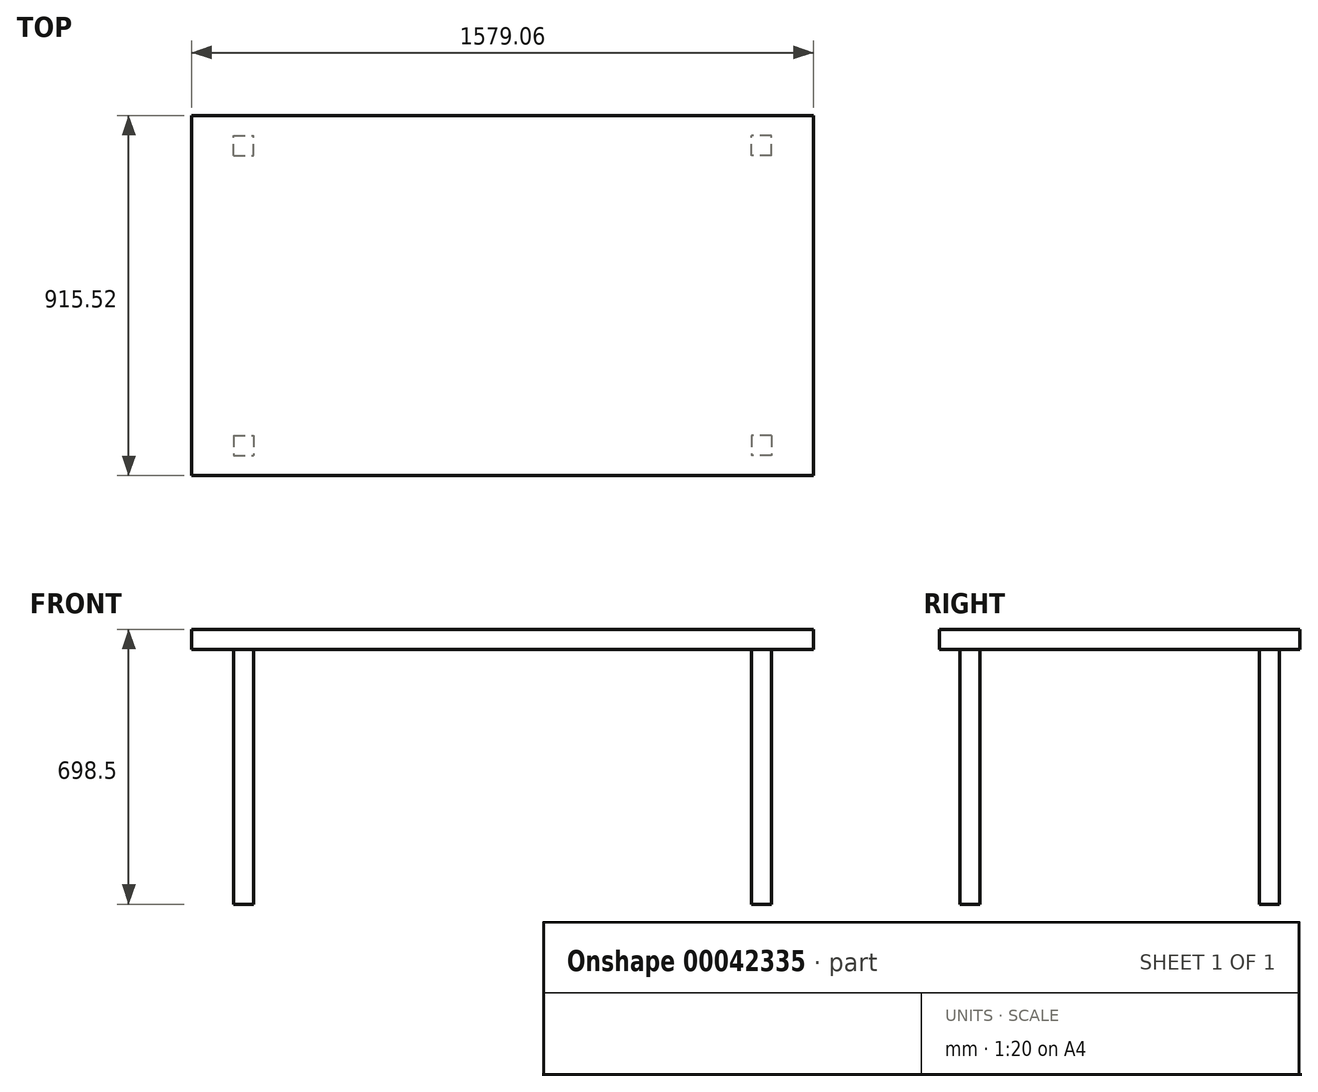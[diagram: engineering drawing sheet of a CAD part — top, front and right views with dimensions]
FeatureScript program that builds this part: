
annotation { "Feature Type Name" : "Feature", "Feature Type Description" : "" }
export const myFeature = defineFeature(function(context is Context, id is Id, definition is map)
    precondition{}
    {
        {
            var Q0;
            Q0=qCreatedBy(makeId("Top.planeOp"),FACE);
            var sketch = newSketch(context, id + "F0", { "sketchPlane" : qUnion([Q0])});
            skLineSegment(sketch, "E0.bottom", {"start": v(-734.47, 457.76) * mm, "end": v(789.53, 457.76) * mm});
            skLineSegment(sketch, "E0.top", {"start": v(-734.47, -456.64) * mm, "end": v(789.53, -456.64) * mm});
            skLineSegment(sketch, "E0.left", {"start": v(-734.47, 457.76) * mm, "end": v(-734.47, -456.64) * mm});
            skLineSegment(sketch, "E0.right", {"start": v(789.53, 457.76) * mm, "end": v(789.53, -456.64) * mm});
            skSolve(sketch);
        }
        {
            var Q0;
            Q0=qSketchRegion(id+"F0",true);
            extrude(context, id + "F1", {"entities" : qUnion([Q0]), "depth" : 50.8 * mm});
        }
        {
            var Q0;
            Q0=makeQuery(id+"F1.opExtrude","CAP_FACE",FACE,{"disambiguationData":[OSD([sQuery(id+"F0.wireOp",EDGE,"E0.bottom"),sQuery(id+"F0.wireOp",EDGE,"E0.top"),sQuery(id+"F0.wireOp",EDGE,"E0.left"),sQuery(id+"F0.wireOp",EDGE,"E0.right")])],"isStart":false});
            var sketch = newSketch(context, id + "F2", { "sketchPlane" : qUnion([Q0])});
            skLineSegment(sketch, "E1.bottom", {"start": v(-683.67, -355.04) * mm, "end": v(-632.87, -355.04) * mm});
            skLineSegment(sketch, "E1.top", {"start": v(-683.67, -405.84) * mm, "end": v(-632.87, -405.84) * mm});
            skLineSegment(sketch, "E1.left", {"start": v(-683.67, -355.04) * mm, "end": v(-683.67, -405.84) * mm});
            skLineSegment(sketch, "E1.right", {"start": v(-632.87, -355.04) * mm, "end": v(-632.87, -405.84) * mm});
            skSolve(sketch);
        }
        {
            var Q0;
            Q0=makeQuery(id+"F2.imprint","IMPRINT",FACE,{"disambiguationData":[TD([[makeQuery(id+"F2.imprint","IMPRINT",EDGE,{"derivedFrom":sQuery(id+"F2.wireOp",EDGE,"E1.bottom")}),-1.0]])]});
            extrude(context, id + "F3", {"entities" : qUnion([Q0]), "operationType" : NewBodyOperationType.ADD, "oppositeDirection" : true, "depth" : 698.5 * mm});
        }
        {
            var Q0;
            Q0=makeQuery(id+"F1.opExtrude","SWEPT_BODY",BODY,{"disambiguationData":[OSD([sQuery(id+"F0.wireOp",EDGE,"E0.bottom"),sQuery(id+"F0.wireOp",EDGE,"E0.top"),sQuery(id+"F0.wireOp",EDGE,"E0.left"),sQuery(id+"F0.wireOp",EDGE,"E0.right")])]});
            var Q1;
            Q1=qCreatedBy(makeId("Front.planeOp"),FACE);
            mirror(context, id + "F4", {"operationType" : NewBodyOperationType.ADD, "entities" : qUnion([Q0]), "mirrorPlane" : qUnion([Q1])});
        }
        {
            var Q0;
            Q0=makeQuery(id+"F1.opExtrude","SWEPT_BODY",BODY,{"disambiguationData":[OSD([sQuery(id+"F0.wireOp",EDGE,"E0.bottom"),sQuery(id+"F0.wireOp",EDGE,"E0.top"),sQuery(id+"F0.wireOp",EDGE,"E0.left"),sQuery(id+"F0.wireOp",EDGE,"E0.right")])]});
            var Q1;
            Q1=qCreatedBy(makeId("Right.planeOp"),FACE);
            mirror(context, id + "F5", {"operationType" : NewBodyOperationType.ADD, "entities" : qUnion([Q0]), "mirrorPlane" : qUnion([Q1])});
        }
    });
